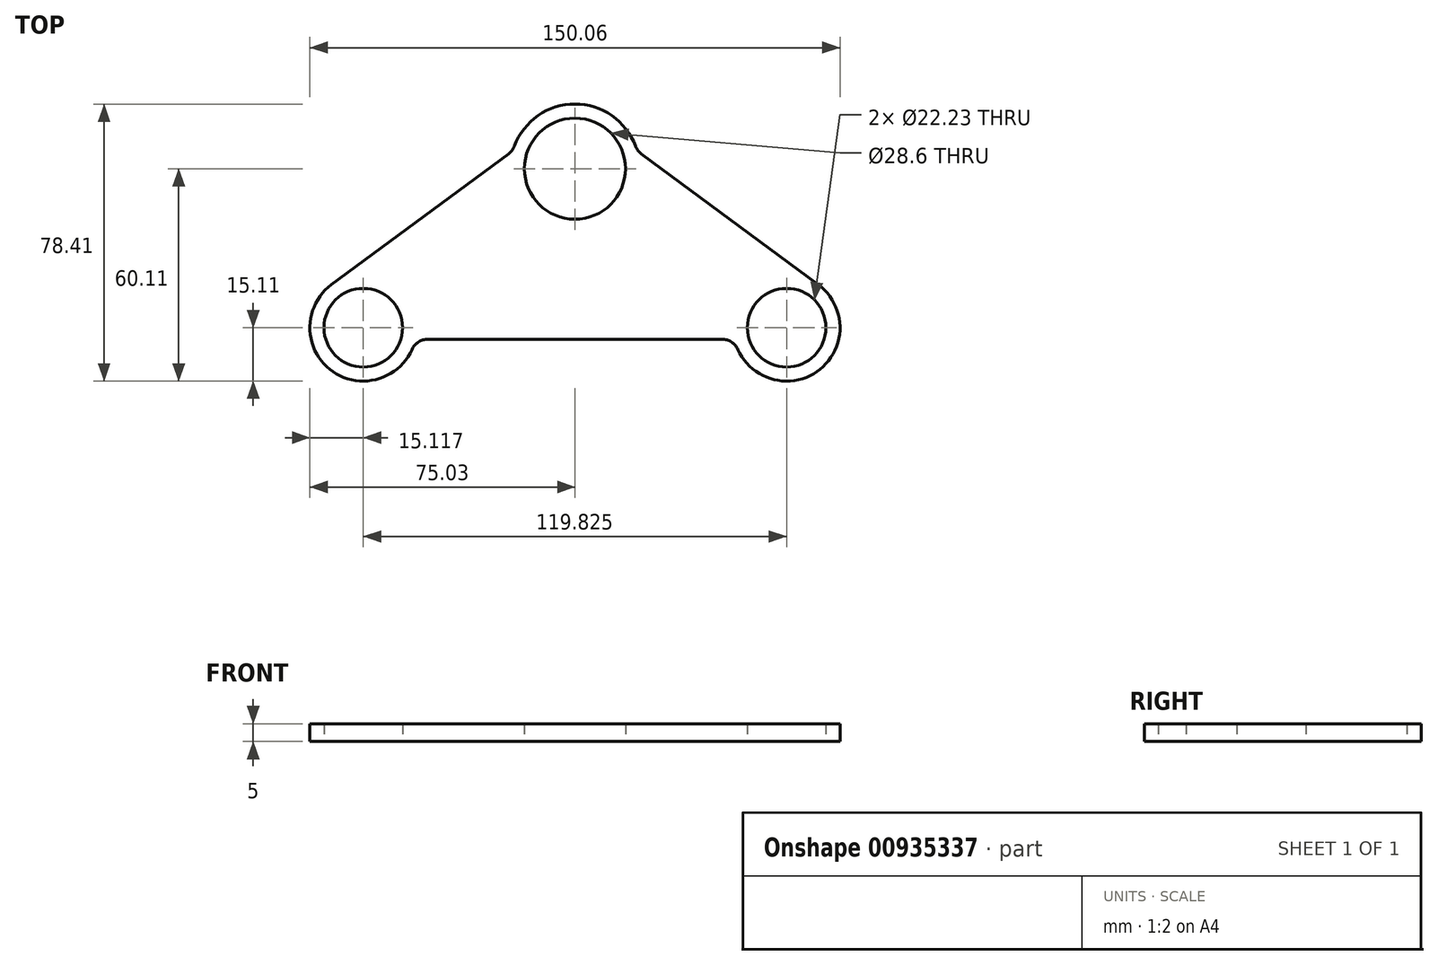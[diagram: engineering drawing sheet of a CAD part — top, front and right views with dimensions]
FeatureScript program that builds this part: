
annotation { "Feature Type Name" : "Feature", "Feature Type Description" : "" }
export const myFeature = defineFeature(function(context is Context, id is Id, definition is map)
    precondition{}
    {
        {
            var Q0;
            Q0=qCreatedBy(makeId("Top.planeOp"),FACE);
            var sketch = newSketch(context, id + "F0", { "sketchPlane" : qUnion([Q0])});
            skCircle(sketch, "E0", {"center": v(-59.91, -45) * mm, "radius": 11.11 * mm});
            skCircle(sketch, "E1", {"center": v(0, 0) * mm, "radius": 14.3 * mm});
            skCircle(sketch, "E2", {"center": v(59.91, -45) * mm, "radius": 11.11 * mm});
            skLineSegment(sketch, "E3", {"start": v(-59.91, -45) * mm, "end": v(59.91, -45) * mm, "construction": true});
            skPoint(sketch, "E4", {"position": v(-48.8, -45) * mm});
            skPoint(sketch, "E5", {"position": v(48.8, -45) * mm});
            skArc(sketch, "E6", {"start": v(-68.9, -32.85) * mm, "mid": v(-69.4, -56.77) * mm, "end": v(-46.13, -51.2) * mm});
            skLineSegment(sketch, "E7", {"start": v(-41.57, -48.25) * mm, "end": v(0, -48.25) * mm});
            skArc(sketch, "E8", {"start": v(0, 18.3) * mm, "mid": v(-10.42, 15.04) * mm, "end": v(-17.14, 6.42) * mm});
            skLineSegment(sketch, "E9", {"start": v(-18.85, 4.16) * mm, "end": v(-68.9, -32.85) * mm});
            skLineSegment(sketch, "E10", {"start": v(0, 18.3) * mm, "end": v(0, 14.3) * mm, "construction": true});
            skLineSegment(sketch, "E11", {"start": v(-71.03, -45) * mm, "end": v(-75.03, -45) * mm, "construction": true});
            skLineSegment(sketch, "E12", {"start": v(-50, -34.73) * mm, "end": v(-50, -45.85) * mm, "construction": true});
            skPoint(sketch, "E13.MirrorP", {"position": v(-51.2, -45) * mm});
            skLineSegment(sketch, "E14.MirrorCS", {"start": v(50, -34.73) * mm, "end": v(50, -45.85) * mm, "construction": true});
            skPoint(sketch, "E15.visualSharp", {"position": v(-45.15, -48.25) * mm});
            skArc(sketch, "E15.filletArc", {"start": v(-41.57, -48.25) * mm, "mid": v(-44.29, -49.05) * mm, "end": v(-46.13, -51.2) * mm});
            skPoint(sketch, "E16.visualSharp", {"position": v(-18.3, 0) * mm});
            skArc(sketch, "E16.filletArc", {"start": v(-18.85, 4.16) * mm, "mid": v(-17.83, 5.17) * mm, "end": v(-17.14, 6.42) * mm});
            skArc(sketch, "E17.MirrorCS", {"start": v(0, 18.3) * mm, "mid": v(10.42, 15.04) * mm, "end": v(17.14, 6.42) * mm});
            skArc(sketch, "E18.MirrorCS", {"start": v(18.85, 4.16) * mm, "mid": v(17.83, 5.17) * mm, "end": v(17.14, 6.42) * mm});
            skLineSegment(sketch, "E19.MirrorCS", {"start": v(18.85, 4.16) * mm, "end": v(68.9, -32.85) * mm});
            skArc(sketch, "E20.MirrorCS", {"start": v(68.9, -32.85) * mm, "mid": v(69.4, -56.77) * mm, "end": v(46.13, -51.2) * mm});
            skArc(sketch, "E21.MirrorCS", {"start": v(41.57, -48.25) * mm, "mid": v(44.29, -49.05) * mm, "end": v(46.13, -51.2) * mm});
            skLineSegment(sketch, "E22.MirrorCS", {"start": v(41.57, -48.25) * mm, "end": v(0, -48.25) * mm});
            skSolve(sketch);
        }
        {
            var Q0;
            Q0=qSketchRegion(id+"F0",true);
            extrude(context, id + "F1", {"entities" : qUnion([Q0]), "endBound" : BoundingType.SYMMETRIC, "depth" : 5 * mm, "offsetDistance" : 25 * mm});
        }
    });
